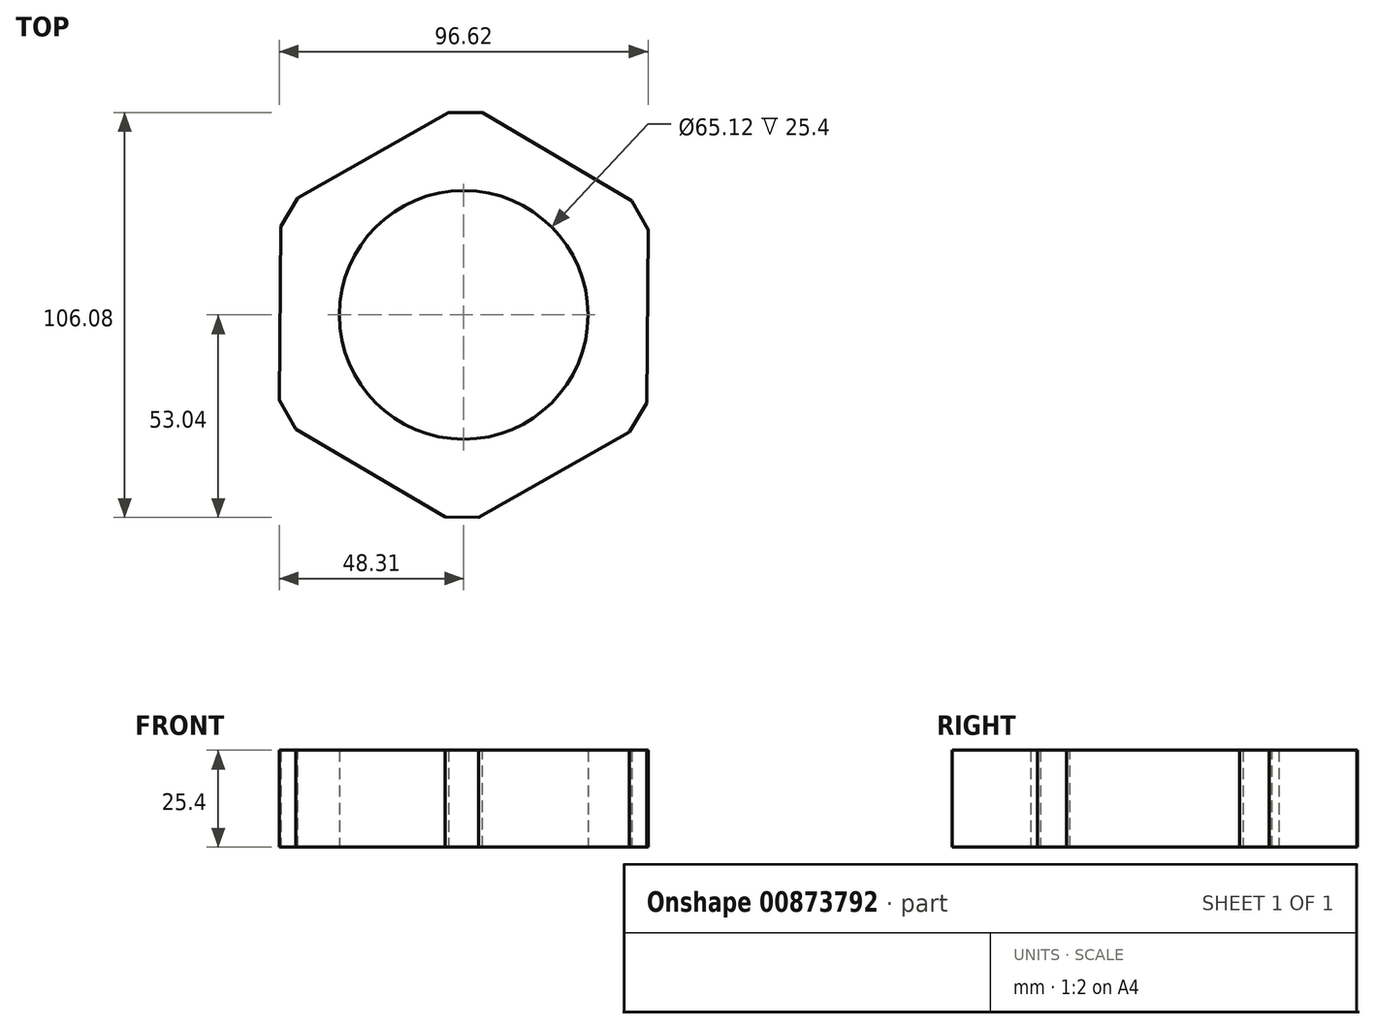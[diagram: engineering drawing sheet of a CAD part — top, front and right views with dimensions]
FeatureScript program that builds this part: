
annotation { "Feature Type Name" : "Feature", "Feature Type Description" : "" }
export const myFeature = defineFeature(function(context is Context, id is Id, definition is map)
    precondition{}
    {
        {
            var Q0;
            Q0=qCreatedBy(makeId("Top.planeOp"),FACE);
            var sketch = newSketch(context, id + "F0", { "sketchPlane" : qUnion([Q0])});
            skCircle(sketch, "E0.cCircle", {"center": v(0, 0) * mm, "radius": 48.1 * mm, "construction": true});
            skLineSegment(sketch, "E0.0", {"start": v(47.86, -28.2) * mm, "end": v(-0.5, -55.55) * mm});
            skLineSegment(sketch, "E0.1", {"start": v(-0.5, -55.55) * mm, "end": v(-48.35, -27.34) * mm});
            skLineSegment(sketch, "E0.2", {"start": v(-48.35, -27.34) * mm, "end": v(-47.86, 28.2) * mm});
            skLineSegment(sketch, "E0.3", {"start": v(-47.86, 28.2) * mm, "end": v(0.5, 55.55) * mm});
            skLineSegment(sketch, "E0.4", {"start": v(0.5, 55.55) * mm, "end": v(48.35, 27.34) * mm});
            skLineSegment(sketch, "E0.5", {"start": v(48.35, 27.34) * mm, "end": v(47.86, -28.2) * mm});
            skPoint(sketch, "E0.0.midPoint", {"position": v(23.68, -41.87) * mm});
            skCircle(sketch, "E1", {"center": v(0, 0) * mm, "radius": 32.56 * mm});
            skSolve(sketch);
        }
        {
            var Q0;
            Q0=makeQuery(id+"F0.imprint","IMPRINT",FACE,{"disambiguationData":[TD([[makeQuery(id+"F0.imprint","IMPRINT",EDGE,{"derivedFrom":sQuery(id+"F0.wireOp",EDGE,"E0.0")}),-1.0]])]});
            extrude(context, id + "F1", {"entities" : qUnion([Q0]), "depth" : 25.4 * mm, "offsetDistance" : 25.4 * mm});
        }
        {
            var Q0;
            Q0=makeQuery(id+"F1.opExtrude","SWEPT_EDGE",EDGE,{"disambiguationData":[OSD([sQuery(id+"F0.wireOp",EDGE,"E0.1"),sQuery(id+"F0.wireOp",EDGE,"E0.2")])]});
            var Q1;
            Q1=makeQuery(id+"F1.opExtrude","SWEPT_EDGE",EDGE,{"disambiguationData":[OSD([sQuery(id+"F0.wireOp",EDGE,"E0.2"),sQuery(id+"F0.wireOp",EDGE,"E0.3")])]});
            var Q2;
            Q2=makeQuery(id+"F1.opExtrude","SWEPT_EDGE",EDGE,{"disambiguationData":[OSD([sQuery(id+"F0.wireOp",EDGE,"E0.0"),sQuery(id+"F0.wireOp",EDGE,"E0.1")])]});
            var Q3;
            Q3=makeQuery(id+"F1.opExtrude","SWEPT_EDGE",EDGE,{"disambiguationData":[OSD([sQuery(id+"F0.wireOp",EDGE,"E0.3"),sQuery(id+"F0.wireOp",EDGE,"E0.4")])]});
            var Q4;
            Q4=makeQuery(id+"F1.opExtrude","SWEPT_EDGE",EDGE,{"disambiguationData":[OSD([sQuery(id+"F0.wireOp",EDGE,"E0.4"),sQuery(id+"F0.wireOp",EDGE,"E0.5")])]});
            var Q5;
            Q5=makeQuery(id+"F1.opExtrude","SWEPT_EDGE",EDGE,{"disambiguationData":[OSD([sQuery(id+"F0.wireOp",EDGE,"E0.0"),sQuery(id+"F0.wireOp",EDGE,"E0.5")])]});
            chamfer(context, id + "F2", {"entities" : qUnion([Q0, Q1, Q2, Q3, Q4, Q5]), "chamferType" : ChamferType.TWO_OFFSETS, "width1" : 5.08 * mm, "oppositeDirection" : false, "width2" : 5.08 * mm, "tangentPropagation" : true});
        }
    });
